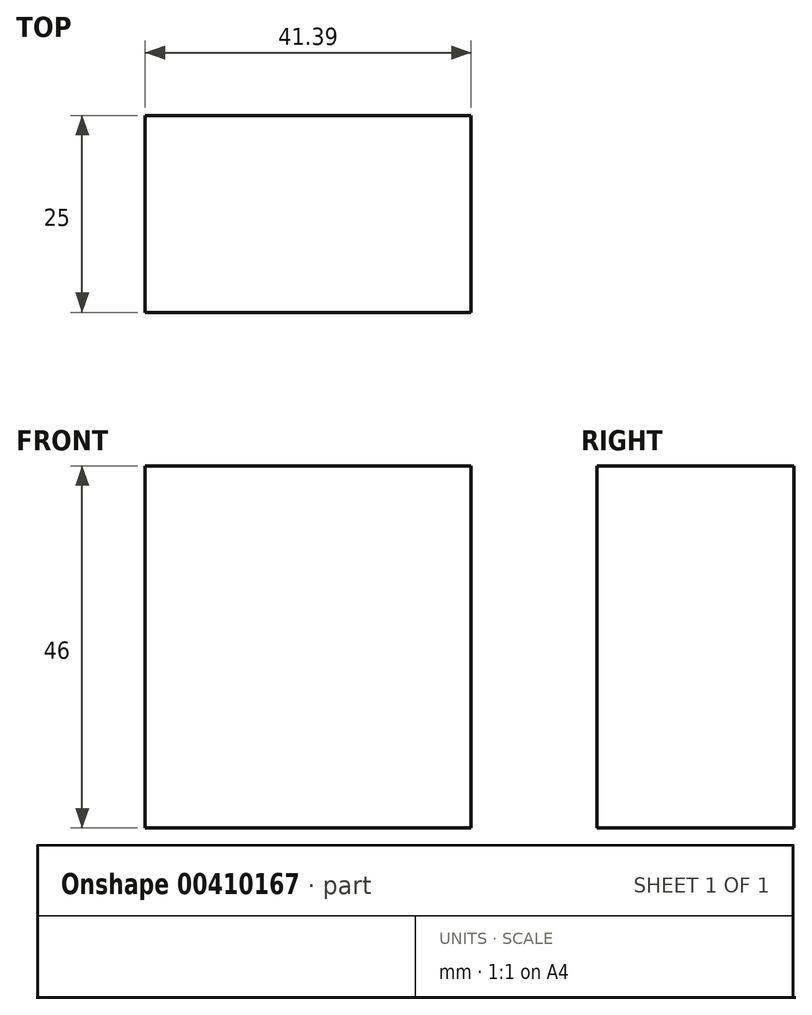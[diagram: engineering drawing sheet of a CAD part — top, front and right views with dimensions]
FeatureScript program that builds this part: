
annotation { "Feature Type Name" : "Feature", "Feature Type Description" : "" }
export const myFeature = defineFeature(function(context is Context, id is Id, definition is map)
    precondition{}
    {
        {
            var Q0;
            Q0=qCreatedBy(makeId("Front.planeOp"),FACE);
            var sketch = newSketch(context, id + "F0", { "sketchPlane" : qUnion([Q0])});
            skLineSegment(sketch, "E0.bottom", {"start": v(-93.8, 14.31) * mm, "end": v(-52.4, 14.31) * mm});
            skLineSegment(sketch, "E0.top", {"start": v(-93.8, 60.3) * mm, "end": v(-52.4, 60.3) * mm});
            skLineSegment(sketch, "E0.left", {"start": v(-93.8, 14.31) * mm, "end": v(-93.8, 60.3) * mm});
            skLineSegment(sketch, "E0.right", {"start": v(-52.4, 14.31) * mm, "end": v(-52.4, 60.3) * mm});
            skPoint(sketch, "E0.middle", {"position": v(-73.1, 37.31) * mm});
            skSolve(sketch);
        }
        {
            var Q0;
            Q0=makeQuery(id+"F0.imprint","IMPRINT",FACE,{"disambiguationData":[TD([[makeQuery(id+"F0.imprint","IMPRINT",EDGE,{"derivedFrom":sQuery(id+"F0.wireOp",EDGE,"E0.bottom")}),1.0]])]});
            extrude(context, id + "F1", {"entities" : qUnion([Q0]), "depth" : 25 * mm});
        }
    });
